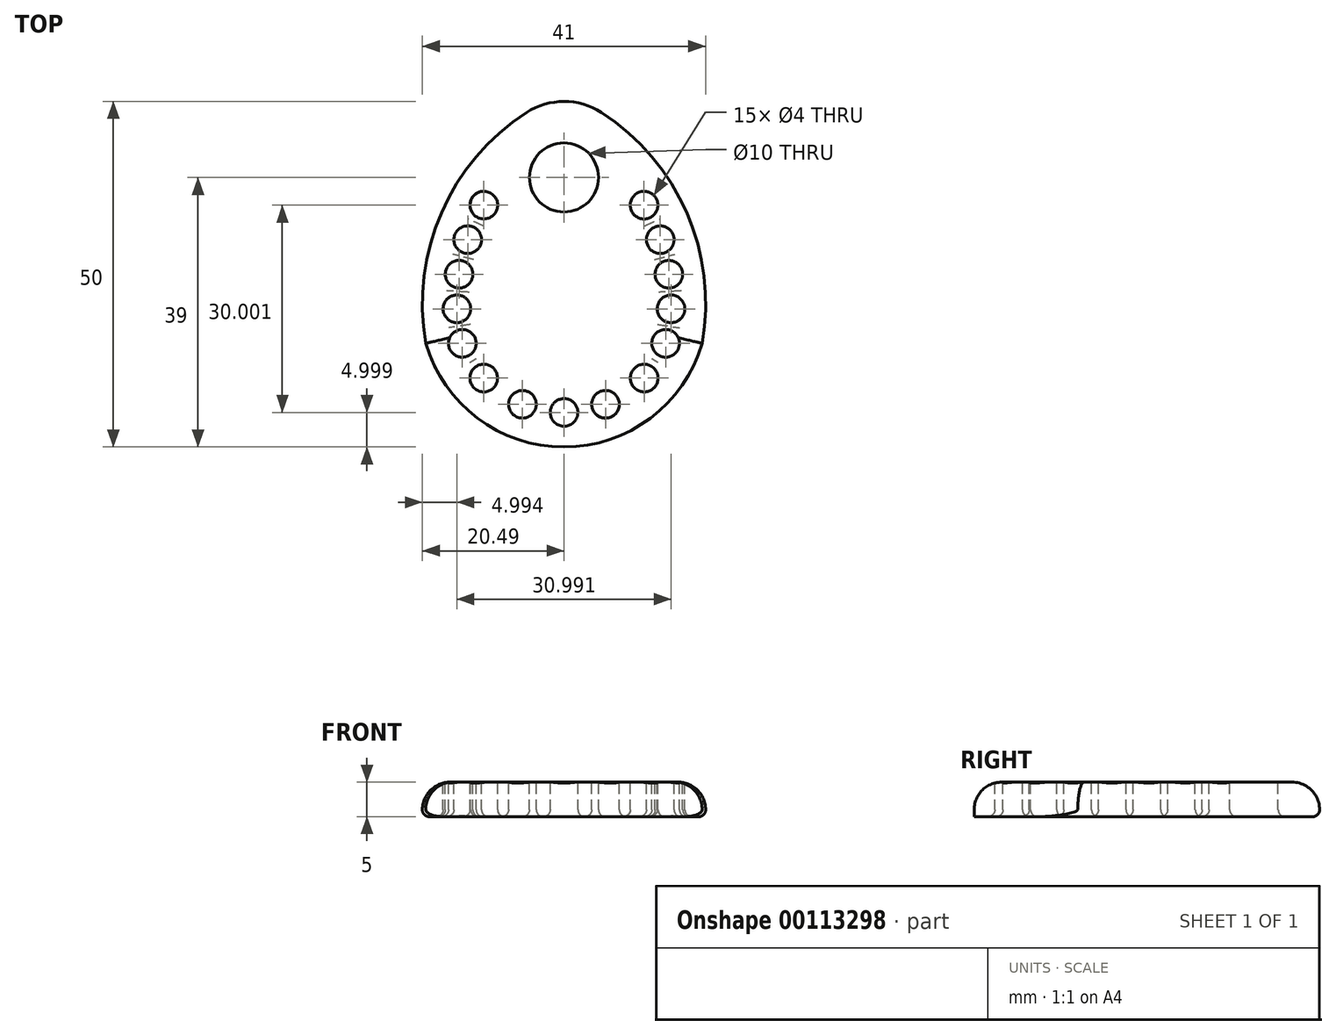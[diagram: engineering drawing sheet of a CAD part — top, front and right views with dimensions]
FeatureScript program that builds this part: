
annotation { "Feature Type Name" : "Feature", "Feature Type Description" : "" }
export const myFeature = defineFeature(function(context is Context, id is Id, definition is map)
    precondition{}
    {
        {
            var Q0;
            Q0=qCreatedBy(makeId("Top.planeOp"),FACE);
            var sketch = newSketch(context, id + "F0", { "sketchPlane" : qUnion([Q0])});
            skLineSegment(sketch, "E0", {"start": v(0, 0) * mm, "end": v(20, 0) * mm, "construction": true});
            skLineSegment(sketch, "E1", {"start": v(0, 0) * mm, "end": v(-20, 0) * mm, "construction": true});
            skLineSegment(sketch, "E2", {"start": v(0, 0) * mm, "end": v(0, 36.23) * mm, "construction": true});
            skLineSegment(sketch, "E3", {"start": v(0, 0) * mm, "end": v(0, -15) * mm, "construction": true});
            skArc(sketch, "E4", {"start": v(-20, 0) * mm, "mid": v(0, -15) * mm, "end": v(20, 0) * mm});
            skArc(sketch, "E5", {"start": v(-5.42, 33.4) * mm, "mid": v(-17.74, 18.9) * mm, "end": v(-20, 0) * mm});
            skArc(sketch, "E6", {"start": v(20, 0) * mm, "mid": v(17.76, 18.9) * mm, "end": v(5.43, 33.4) * mm});
            skPoint(sketch, "E7.visualSharp", {"position": v(0, 36.23) * mm});
            skArc(sketch, "E7.filletArc", {"start": v(5.43, 33.4) * mm, "mid": v(0, 35) * mm, "end": v(-5.42, 33.4) * mm});
            skSolve(sketch);
        }
        {
            var Q0;
            Q0=makeQuery(id+"F0.imprint","IMPRINT",FACE,{"disambiguationData":[TD([[makeQuery(id+"F0.imprint","IMPRINT",EDGE,{"derivedFrom":sQuery(id+"F0.wireOp",EDGE,"E4")}),1.0]])]});
            extrude(context, id + "F1", {"entities" : qUnion([Q0]), "depth" : 5 * mm});
        }
        {
            var Q0;
            Q0=makeQuery(id+"F1.opExtrude","CAP_FACE",FACE,{"disambiguationData":[OSD([sQuery(id+"F0.wireOp",EDGE,"E4"),sQuery(id+"F0.wireOp",EDGE,"E5"),sQuery(id+"F0.wireOp",EDGE,"E6"),sQuery(id+"F0.wireOp",EDGE,"E7.filletArc")])],"isStart":false});
            var sketch = newSketch(context, id + "F2", { "sketchPlane" : qUnion([Q0])});
            skArc(sketch, "E8.0", {"start": v(-2.7, 29.2) * mm, "mid": v(-13.1, 17.02) * mm, "end": v(-15.12, 1.14) * mm, "construction": true});
            skArc(sketch, "E8.1", {"start": v(2.72, 29.2) * mm, "mid": v(0, 30) * mm, "end": v(-2.7, 29.2) * mm, "construction": true});
            skArc(sketch, "E8.2", {"start": v(15.12, 1.15) * mm, "mid": v(13.12, 17.03) * mm, "end": v(2.72, 29.2) * mm, "construction": true});
            skArc(sketch, "E8.3", {"start": v(-15.12, 1.14) * mm, "mid": v(0, -10) * mm, "end": v(15.12, 1.15) * mm, "construction": true});
            skCircle(sketch, "E9", {"center": v(0, 24) * mm, "radius": 5 * mm});
            skLineSegment(sketch, "E10", {"start": v(-22.93, 0) * mm, "end": v(24.82, 0) * mm, "construction": true});
            skLineSegment(sketch, "E11.0", {"start": v(-22.93, -5) * mm, "end": v(24.82, -5) * mm, "construction": true});
            skLineSegment(sketch, "E12.0", {"start": v(-22.93, -10) * mm, "end": v(24.82, -10) * mm, "construction": true});
            skLineSegment(sketch, "E13.0", {"start": v(-22.93, 5) * mm, "end": v(24.82, 5) * mm, "construction": true});
            skLineSegment(sketch, "E14.0", {"start": v(-22.93, 10) * mm, "end": v(24.82, 10) * mm, "construction": true});
            skLineSegment(sketch, "E15.0", {"start": v(-22.93, 15) * mm, "end": v(24.82, 15) * mm, "construction": true});
            skLineSegment(sketch, "E16.0", {"start": v(-22.93, 20) * mm, "end": v(24.82, 20) * mm, "construction": true});
            skCircle(sketch, "E17", {"center": v(11.6, 20) * mm, "radius": 2 * mm});
            skCircle(sketch, "E18", {"center": v(13.93, 15) * mm, "radius": 2 * mm});
            skCircle(sketch, "E19", {"center": v(15.18, 10) * mm, "radius": 2 * mm});
            skCircle(sketch, "E20", {"center": v(15.5, 5) * mm, "radius": 2 * mm});
            skCircle(sketch, "E21", {"center": v(14.71, 0) * mm, "radius": 2 * mm});
            skCircle(sketch, "E22", {"center": v(11.61, -5.03) * mm, "radius": 2 * mm});
            skLineSegment(sketch, "E23", {"start": v(0, 0) * mm, "end": v(0, -10) * mm, "construction": true});
            skCircle(sketch, "E24", {"center": v(0.01, -10) * mm, "radius": 2 * mm});
            skLineSegment(sketch, "E25.0", {"start": v(6, 0) * mm, "end": v(6, -10) * mm, "construction": true});
            skCircle(sketch, "E26", {"center": v(6.01, -8.82) * mm, "radius": 2 * mm});
            skCircle(sketch, "E27.MirrorC", {"center": v(-11.6, 20) * mm, "radius": 2 * mm});
            skCircle(sketch, "E28.MirrorC", {"center": v(-13.93, 15) * mm, "radius": 2 * mm});
            skCircle(sketch, "E29.MirrorC", {"center": v(-15.18, 10) * mm, "radius": 2 * mm});
            skCircle(sketch, "E30.MirrorC", {"center": v(-15.5, 5) * mm, "radius": 2 * mm});
            skCircle(sketch, "E31.MirrorC", {"center": v(-14.71, 0) * mm, "radius": 2 * mm});
            skCircle(sketch, "E32.MirrorC", {"center": v(-11.61, -5.03) * mm, "radius": 2 * mm});
            skCircle(sketch, "E33.MirrorC", {"center": v(-6.01, -8.82) * mm, "radius": 2 * mm});
            skSolve(sketch);
        }
        {
            var Q0;
            Q0 = qSketchRegion(id + "F2", true);
            var Q1;
            Q1 = qConstructionFilter(qBodyType(qCreatedBy(id + "F2" ,EDGE), BodyType.WIRE), ConstructionObject.NO);
            extrude(context, id + "F3", {"entities" : qUnion([Q0]), "operationType" : NewBodyOperationType.REMOVE, "surfaceEntities" : qUnion([Q1]), "endBound" : BoundingType.THROUGH_ALL, "oppositeDirection" : true, "depth" : 25 * mm});
        }
        {
            var Q0;
            Q0=makeQuery(id+"F1.opExtrude","CAP_EDGE",EDGE,{"disambiguationData":[OSD([sQuery(id+"F0.wireOp",EDGE,"E5")])],"isStart":false});
            var Q1;
            Q1=makeQuery(id+"F1.opExtrude","CAP_EDGE",EDGE,{"disambiguationData":[OSD([sQuery(id+"F0.wireOp",EDGE,"E7.filletArc")])],"isStart":false});
            var Q2;
            Q2=makeQuery(id+"F1.opExtrude","CAP_EDGE",EDGE,{"disambiguationData":[OSD([sQuery(id+"F0.wireOp",EDGE,"E6")])],"isStart":false});
            var Q3;
            Q3=makeQuery(id+"F1.opExtrude","CAP_EDGE",EDGE,{"disambiguationData":[OSD([sQuery(id+"F0.wireOp",EDGE,"E4")])],"isStart":false});
            var Q4;
            Q4=makeQuery(id+"F3.boolean.opBoolean","COPY",EDGE,{"derivedFrom":makeQuery(id+"F3.opExtrude","CAP_EDGE",EDGE,{"disambiguationData":[OSD([sQuery(id+"F2.wireOp",EDGE,"E9")])],"isStart":true})});
            fillet(context, id + "F4", {"entities" : qUnion([Q0, Q1, Q2, Q3, Q4]), "radius" : 4 * mm, "tangentPropagation" : true, "allowEdgeOverflow" : false});
        }
        {
            var Q0;
            Q0=makeQuery(id+"F1.opExtrude","CAP_EDGE",EDGE,{"disambiguationData":[OSD([sQuery(id+"F0.wireOp",EDGE,"E6")])],"isStart":true});
            var Q1;
            Q1=makeQuery(id+"F3.boolean.opBoolean","INTERSECT",EDGE,{"derivedFrom":[makeQuery(id+"F1.opExtrude","CAP_FACE",FACE,{"disambiguationData":[OSD([sQuery(id+"F0.wireOp",EDGE,"E4"),sQuery(id+"F0.wireOp",EDGE,"E5"),sQuery(id+"F0.wireOp",EDGE,"E6"),sQuery(id+"F0.wireOp",EDGE,"E7.filletArc")])],"isStart":true}),makeQuery(id+"F3.opExtrude","SWEPT_FACE",FACE,{"disambiguationData":[OSD([sQuery(id+"F2.wireOp",EDGE,"E9")])]})]});
            var Q2;
            Q2=makeQuery(id+"F3.boolean.opBoolean","INTERSECT",EDGE,{"derivedFrom":[makeQuery(id+"F1.opExtrude","CAP_FACE",FACE,{"disambiguationData":[OSD([sQuery(id+"F0.wireOp",EDGE,"E4"),sQuery(id+"F0.wireOp",EDGE,"E5"),sQuery(id+"F0.wireOp",EDGE,"E6"),sQuery(id+"F0.wireOp",EDGE,"E7.filletArc")])],"isStart":true}),makeQuery(id+"F3.opExtrude","SWEPT_FACE",FACE,{"disambiguationData":[OSD([sQuery(id+"F2.wireOp",EDGE,"E17")])]})]});
            var Q3;
            Q3=makeQuery(id+"F3.boolean.opBoolean","INTERSECT",EDGE,{"derivedFrom":[makeQuery(id+"F1.opExtrude","CAP_FACE",FACE,{"disambiguationData":[OSD([sQuery(id+"F0.wireOp",EDGE,"E4"),sQuery(id+"F0.wireOp",EDGE,"E5"),sQuery(id+"F0.wireOp",EDGE,"E6"),sQuery(id+"F0.wireOp",EDGE,"E7.filletArc")])],"isStart":true}),makeQuery(id+"F3.opExtrude","SWEPT_FACE",FACE,{"disambiguationData":[OSD([sQuery(id+"F2.wireOp",EDGE,"E18")])]})]});
            var Q4;
            Q4=makeQuery(id+"F3.boolean.opBoolean","INTERSECT",EDGE,{"derivedFrom":[makeQuery(id+"F1.opExtrude","CAP_FACE",FACE,{"disambiguationData":[OSD([sQuery(id+"F0.wireOp",EDGE,"E4"),sQuery(id+"F0.wireOp",EDGE,"E5"),sQuery(id+"F0.wireOp",EDGE,"E6"),sQuery(id+"F0.wireOp",EDGE,"E7.filletArc")])],"isStart":true}),makeQuery(id+"F3.opExtrude","SWEPT_FACE",FACE,{"disambiguationData":[OSD([sQuery(id+"F2.wireOp",EDGE,"E19")])]})]});
            var Q5;
            Q5=makeQuery(id+"F3.boolean.opBoolean","INTERSECT",EDGE,{"derivedFrom":[makeQuery(id+"F1.opExtrude","CAP_FACE",FACE,{"disambiguationData":[OSD([sQuery(id+"F0.wireOp",EDGE,"E4"),sQuery(id+"F0.wireOp",EDGE,"E5"),sQuery(id+"F0.wireOp",EDGE,"E6"),sQuery(id+"F0.wireOp",EDGE,"E7.filletArc")])],"isStart":true}),makeQuery(id+"F3.opExtrude","SWEPT_FACE",FACE,{"disambiguationData":[OSD([sQuery(id+"F2.wireOp",EDGE,"E20")])]})]});
            var Q6;
            Q6=makeQuery(id+"F3.boolean.opBoolean","INTERSECT",EDGE,{"derivedFrom":[makeQuery(id+"F1.opExtrude","CAP_FACE",FACE,{"disambiguationData":[OSD([sQuery(id+"F0.wireOp",EDGE,"E4"),sQuery(id+"F0.wireOp",EDGE,"E5"),sQuery(id+"F0.wireOp",EDGE,"E6"),sQuery(id+"F0.wireOp",EDGE,"E7.filletArc")])],"isStart":true}),makeQuery(id+"F3.opExtrude","SWEPT_FACE",FACE,{"disambiguationData":[OSD([sQuery(id+"F2.wireOp",EDGE,"E21")])]})]});
            var Q7;
            Q7=makeQuery(id+"F3.boolean.opBoolean","INTERSECT",EDGE,{"derivedFrom":[makeQuery(id+"F1.opExtrude","CAP_FACE",FACE,{"disambiguationData":[OSD([sQuery(id+"F0.wireOp",EDGE,"E4"),sQuery(id+"F0.wireOp",EDGE,"E5"),sQuery(id+"F0.wireOp",EDGE,"E6"),sQuery(id+"F0.wireOp",EDGE,"E7.filletArc")])],"isStart":true}),makeQuery(id+"F3.opExtrude","SWEPT_FACE",FACE,{"disambiguationData":[OSD([sQuery(id+"F2.wireOp",EDGE,"E22")])]})]});
            var Q8;
            Q8=makeQuery(id+"F3.boolean.opBoolean","INTERSECT",EDGE,{"derivedFrom":[makeQuery(id+"F1.opExtrude","CAP_FACE",FACE,{"disambiguationData":[OSD([sQuery(id+"F0.wireOp",EDGE,"E4"),sQuery(id+"F0.wireOp",EDGE,"E5"),sQuery(id+"F0.wireOp",EDGE,"E6"),sQuery(id+"F0.wireOp",EDGE,"E7.filletArc")])],"isStart":true}),makeQuery(id+"F3.opExtrude","SWEPT_FACE",FACE,{"disambiguationData":[OSD([sQuery(id+"F2.wireOp",EDGE,"E26")])]})]});
            var Q9;
            Q9=makeQuery(id+"F3.boolean.opBoolean","INTERSECT",EDGE,{"derivedFrom":[makeQuery(id+"F1.opExtrude","CAP_FACE",FACE,{"disambiguationData":[OSD([sQuery(id+"F0.wireOp",EDGE,"E4"),sQuery(id+"F0.wireOp",EDGE,"E5"),sQuery(id+"F0.wireOp",EDGE,"E6"),sQuery(id+"F0.wireOp",EDGE,"E7.filletArc")])],"isStart":true}),makeQuery(id+"F3.opExtrude","SWEPT_FACE",FACE,{"disambiguationData":[OSD([sQuery(id+"F2.wireOp",EDGE,"E24")])]})]});
            var Q10;
            Q10=makeQuery(id+"F3.boolean.opBoolean","INTERSECT",EDGE,{"derivedFrom":[makeQuery(id+"F1.opExtrude","CAP_FACE",FACE,{"disambiguationData":[OSD([sQuery(id+"F0.wireOp",EDGE,"E4"),sQuery(id+"F0.wireOp",EDGE,"E5"),sQuery(id+"F0.wireOp",EDGE,"E6"),sQuery(id+"F0.wireOp",EDGE,"E7.filletArc")])],"isStart":true}),makeQuery(id+"F3.opExtrude","SWEPT_FACE",FACE,{"disambiguationData":[OSD([sQuery(id+"F2.wireOp",EDGE,"E33.MirrorC")])]})]});
            var Q11;
            Q11=makeQuery(id+"F3.boolean.opBoolean","INTERSECT",EDGE,{"derivedFrom":[makeQuery(id+"F1.opExtrude","CAP_FACE",FACE,{"disambiguationData":[OSD([sQuery(id+"F0.wireOp",EDGE,"E4"),sQuery(id+"F0.wireOp",EDGE,"E5"),sQuery(id+"F0.wireOp",EDGE,"E6"),sQuery(id+"F0.wireOp",EDGE,"E7.filletArc")])],"isStart":true}),makeQuery(id+"F3.opExtrude","SWEPT_FACE",FACE,{"disambiguationData":[OSD([sQuery(id+"F2.wireOp",EDGE,"E32.MirrorC")])]})]});
            var Q12;
            Q12=makeQuery(id+"F3.boolean.opBoolean","INTERSECT",EDGE,{"derivedFrom":[makeQuery(id+"F1.opExtrude","CAP_FACE",FACE,{"disambiguationData":[OSD([sQuery(id+"F0.wireOp",EDGE,"E4"),sQuery(id+"F0.wireOp",EDGE,"E5"),sQuery(id+"F0.wireOp",EDGE,"E6"),sQuery(id+"F0.wireOp",EDGE,"E7.filletArc")])],"isStart":true}),makeQuery(id+"F3.opExtrude","SWEPT_FACE",FACE,{"disambiguationData":[OSD([sQuery(id+"F2.wireOp",EDGE,"E31.MirrorC")])]})]});
            var Q13;
            Q13=makeQuery(id+"F3.boolean.opBoolean","INTERSECT",EDGE,{"derivedFrom":[makeQuery(id+"F1.opExtrude","CAP_FACE",FACE,{"disambiguationData":[OSD([sQuery(id+"F0.wireOp",EDGE,"E4"),sQuery(id+"F0.wireOp",EDGE,"E5"),sQuery(id+"F0.wireOp",EDGE,"E6"),sQuery(id+"F0.wireOp",EDGE,"E7.filletArc")])],"isStart":true}),makeQuery(id+"F3.opExtrude","SWEPT_FACE",FACE,{"disambiguationData":[OSD([sQuery(id+"F2.wireOp",EDGE,"E30.MirrorC")])]})]});
            var Q14;
            Q14=makeQuery(id+"F3.boolean.opBoolean","INTERSECT",EDGE,{"derivedFrom":[makeQuery(id+"F1.opExtrude","CAP_FACE",FACE,{"disambiguationData":[OSD([sQuery(id+"F0.wireOp",EDGE,"E4"),sQuery(id+"F0.wireOp",EDGE,"E5"),sQuery(id+"F0.wireOp",EDGE,"E6"),sQuery(id+"F0.wireOp",EDGE,"E7.filletArc")])],"isStart":true}),makeQuery(id+"F3.opExtrude","SWEPT_FACE",FACE,{"disambiguationData":[OSD([sQuery(id+"F2.wireOp",EDGE,"E29.MirrorC")])]})]});
            var Q15;
            Q15=makeQuery(id+"F3.boolean.opBoolean","INTERSECT",EDGE,{"derivedFrom":[makeQuery(id+"F1.opExtrude","CAP_FACE",FACE,{"disambiguationData":[OSD([sQuery(id+"F0.wireOp",EDGE,"E4"),sQuery(id+"F0.wireOp",EDGE,"E5"),sQuery(id+"F0.wireOp",EDGE,"E6"),sQuery(id+"F0.wireOp",EDGE,"E7.filletArc")])],"isStart":true}),makeQuery(id+"F3.opExtrude","SWEPT_FACE",FACE,{"disambiguationData":[OSD([sQuery(id+"F2.wireOp",EDGE,"E28.MirrorC")])]})]});
            var Q16;
            Q16=makeQuery(id+"F3.boolean.opBoolean","INTERSECT",EDGE,{"derivedFrom":[makeQuery(id+"F1.opExtrude","CAP_FACE",FACE,{"disambiguationData":[OSD([sQuery(id+"F0.wireOp",EDGE,"E4"),sQuery(id+"F0.wireOp",EDGE,"E5"),sQuery(id+"F0.wireOp",EDGE,"E6"),sQuery(id+"F0.wireOp",EDGE,"E7.filletArc")])],"isStart":true}),makeQuery(id+"F3.opExtrude","SWEPT_FACE",FACE,{"disambiguationData":[OSD([sQuery(id+"F2.wireOp",EDGE,"E27.MirrorC")])]})]});
            fillet(context, id + "F5", {"entities" : qUnion([Q0, Q1, Q2, Q3, Q4, Q5, Q6, Q7, Q8, Q9, Q10, Q11, Q12, Q13, Q14, Q15, Q16]), "radius" : 1 * mm, "tangentPropagation" : true, "allowEdgeOverflow" : false});
        }
    });
